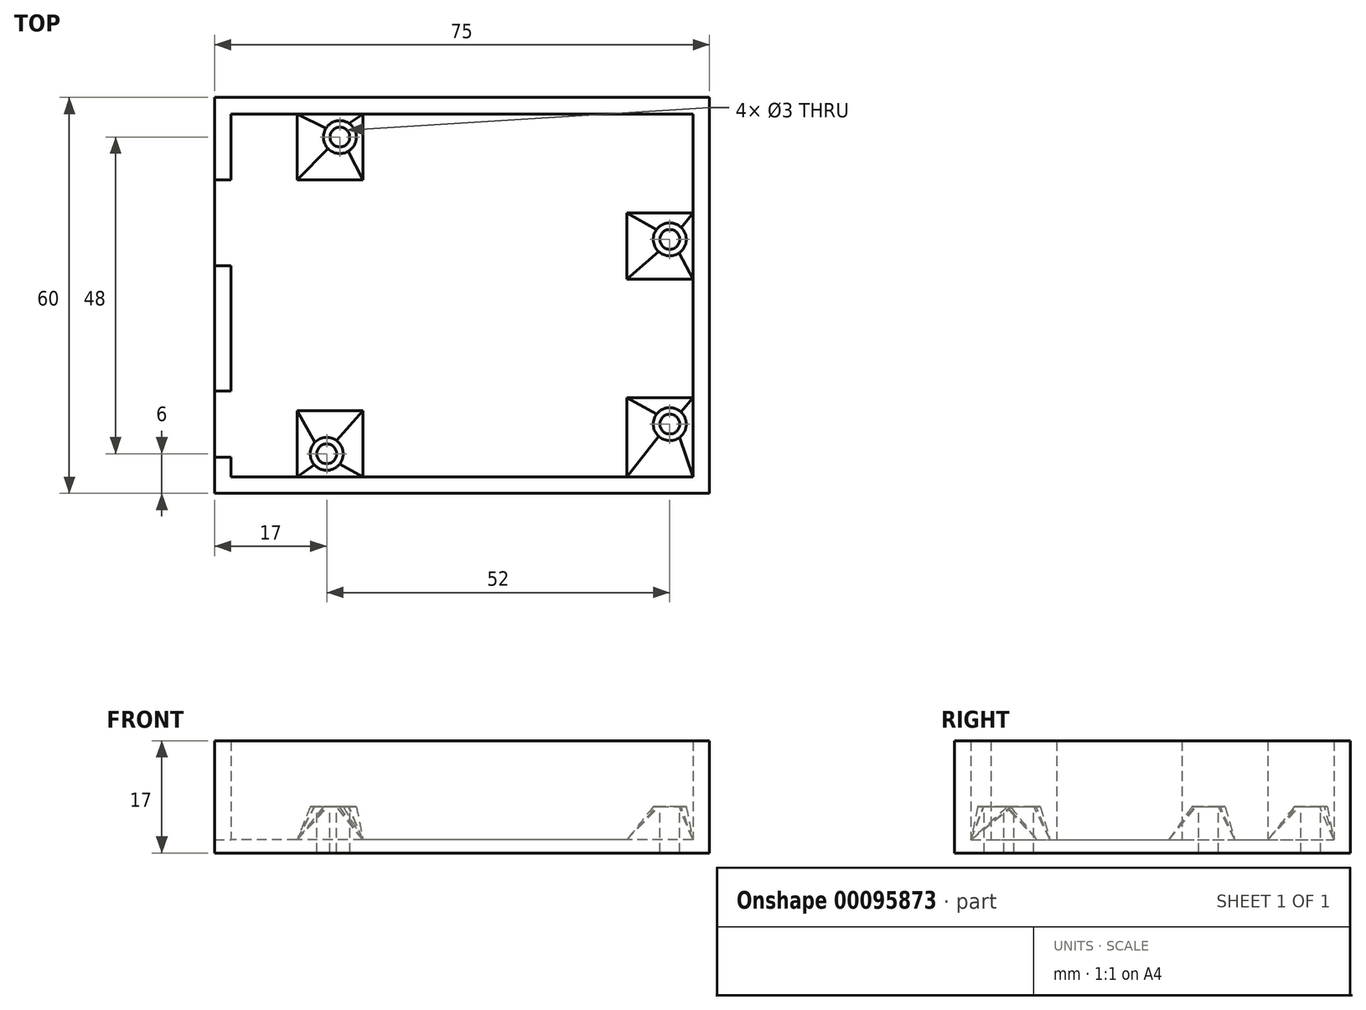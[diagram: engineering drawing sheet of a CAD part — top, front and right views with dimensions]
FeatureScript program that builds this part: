
annotation { "Feature Type Name" : "Feature", "Feature Type Description" : "" }
export const myFeature = defineFeature(function(context is Context, id is Id, definition is map)
    precondition{}
    {
        {
            var Q0;
            Q0=qCreatedBy(makeId("Top.planeOp"),FACE);
            var sketch = newSketch(context, id + "F0", { "sketchPlane" : qUnion([Q0])});
            skLineSegment(sketch, "E0.rect.bottom", {"start": v(37.5, -30) * mm, "end": v(-37.5, -30) * mm});
            skLineSegment(sketch, "E0.rect.top", {"start": v(37.5, 30) * mm, "end": v(-37.5, 30) * mm});
            skLineSegment(sketch, "E0.rect.left", {"start": v(37.5, -30) * mm, "end": v(37.5, 30) * mm});
            skLineSegment(sketch, "E0.rect.right", {"start": v(-37.5, -30) * mm, "end": v(-37.5, 30) * mm});
            skPoint(sketch, "E0.rect.middle", {"position": v(0, 0) * mm});
            skSolve(sketch);
        }
        {
            var Q0;
            Q0=qSketchRegion(id+"F0",true);
            extrude(context, id + "F1", {"entities" : qUnion([Q0]), "depth" : 2 * mm});
        }
        {
            var Q0;
            Q0=makeQuery(id+"F1.opExtrude","CAP_FACE",FACE,{"disambiguationData":[OSD([sQuery(id+"F0.wireOp",EDGE,"E0.rect.bottom"),sQuery(id+"F0.wireOp",EDGE,"E0.rect.top"),sQuery(id+"F0.wireOp",EDGE,"E0.rect.left"),sQuery(id+"F0.wireOp",EDGE,"E0.rect.right")])],"isStart":false});
            var sketch = newSketch(context, id + "F2", { "sketchPlane" : qUnion([Q0])});
            skLineSegment(sketch, "E1.rect.bottom", {"start": v(35, -27.5) * mm, "end": v(-35, -27.5) * mm});
            skLineSegment(sketch, "E1.rect.top", {"start": v(35, 27.5) * mm, "end": v(-35, 27.5) * mm});
            skLineSegment(sketch, "E1.rect.left", {"start": v(35, -27.5) * mm, "end": v(35, 27.5) * mm});
            skLineSegment(sketch, "E1.rect.right", {"start": v(-35, -27.5) * mm, "end": v(-35, 27.5) * mm});
            skPoint(sketch, "E1.rect.middle", {"position": v(0, 0) * mm});
            skLineSegment(sketch, "E2.rect.bottom", {"start": v(37.5, -30) * mm, "end": v(-37.5, -30) * mm});
            skLineSegment(sketch, "E2.rect.top", {"start": v(37.5, 30) * mm, "end": v(-37.5, 30) * mm});
            skLineSegment(sketch, "E2.rect.left", {"start": v(37.5, -30) * mm, "end": v(37.5, 30) * mm});
            skLineSegment(sketch, "E2.rect.right", {"start": v(-37.5, -30) * mm, "end": v(-37.5, 30) * mm});
            skSolve(sketch);
        }
        {
            var Q0;
            Q0=qSketchRegion(id+"F2",true);
            extrude(context, id + "F3", {"entities" : qUnion([Q0]), "operationType" : NewBodyOperationType.ADD, "depth" : 15 * mm});
        }
        {
            var Q0;
            Q0=makeQuery(id+"F1.opExtrude","CAP_FACE",FACE,{"disambiguationData":[OSD([sQuery(id+"F0.wireOp",EDGE,"E0.rect.bottom"),sQuery(id+"F0.wireOp",EDGE,"E0.rect.top"),sQuery(id+"F0.wireOp",EDGE,"E0.rect.left"),sQuery(id+"F0.wireOp",EDGE,"E0.rect.right")])],"isStart":false});
            var sketch = newSketch(context, id + "F4", { "sketchPlane" : qUnion([Q0])});
            skLineSegment(sketch, "E3.bottom", {"start": v(-25, 27.5) * mm, "end": v(-15, 27.5) * mm});
            skLineSegment(sketch, "E3.top", {"start": v(-25, 17.5) * mm, "end": v(-15, 17.5) * mm});
            skLineSegment(sketch, "E3.left", {"start": v(-25, 27.5) * mm, "end": v(-25, 17.5) * mm});
            skLineSegment(sketch, "E3.right", {"start": v(-15, 27.5) * mm, "end": v(-15, 17.5) * mm});
            skLineSegment(sketch, "E4.bottom", {"start": v(-25, -27.5) * mm, "end": v(-15, -27.5) * mm});
            skLineSegment(sketch, "E4.top", {"start": v(-25, -17.5) * mm, "end": v(-15, -17.5) * mm});
            skLineSegment(sketch, "E4.left", {"start": v(-25, -27.5) * mm, "end": v(-25, -17.5) * mm});
            skLineSegment(sketch, "E4.right", {"start": v(-15, -27.5) * mm, "end": v(-15, -17.5) * mm});
            skLineSegment(sketch, "E5.bottom", {"start": v(35, -27.5) * mm, "end": v(25, -27.5) * mm});
            skLineSegment(sketch, "E5.top", {"start": v(35, -15.5) * mm, "end": v(25, -15.5) * mm});
            skLineSegment(sketch, "E5.left", {"start": v(35, -27.5) * mm, "end": v(35, -15.5) * mm});
            skLineSegment(sketch, "E5.right", {"start": v(25, -27.5) * mm, "end": v(25, -15.5) * mm});
            skLineSegment(sketch, "E6.bottom", {"start": v(35, 12.5) * mm, "end": v(25, 12.5) * mm});
            skLineSegment(sketch, "E6.top", {"start": v(35, 2.5) * mm, "end": v(25, 2.5) * mm});
            skLineSegment(sketch, "E6.left", {"start": v(35, 12.5) * mm, "end": v(35, 2.5) * mm});
            skLineSegment(sketch, "E6.right", {"start": v(25, 12.5) * mm, "end": v(25, 2.5) * mm});
            skSolve(sketch);
        }
        {
            var Q0;
            Q0=makeQuery(id+"F4.imprint","IMPRINT",FACE,{"disambiguationData":[TD([[makeQuery(id+"F4.imprint","IMPRINT",EDGE,{"derivedFrom":sQuery(id+"F4.wireOp",EDGE,"E3.top")}),-1.0]])]});
            cPlane(context, id + "F5", {"entities" : qUnion([Q0]), "cplaneType" : CPlaneType.OFFSET, "offset" : 5 * mm, "width" : 150 * mm, "height" : 150 * mm});
        }
        {
            var Q0;
            Q0=qCreatedBy(id+"F5.planeOp",FACE);
            var sketch = newSketch(context, id + "F6", { "sketchPlane" : qUnion([Q0])});
            skArc(sketch, "E7", {"start": v(-17.2, 21.86) * mm, "mid": v(-16, 23.94) * mm, "end": v(-17.1, 26.07) * mm});
            skArc(sketch, "E8", {"start": v(-17.1, 26.07) * mm, "mid": v(-19, 26.45) * mm, "end": v(-20.6, 25.36) * mm});
            skArc(sketch, "E9", {"start": v(-20.6, 25.36) * mm, "mid": v(-20.99, 23.76) * mm, "end": v(-20.3, 22.26) * mm});
            skArc(sketch, "E10", {"start": v(-20.3, 22.26) * mm, "mid": v(-18.82, 21.52) * mm, "end": v(-17.2, 21.86) * mm});
            skArc(sketch, "E11", {"start": v(-22.3, -22.26) * mm, "mid": v(-23, -23.92) * mm, "end": v(-22.4, -25.63) * mm});
            skArc(sketch, "E12", {"start": v(-19.03, -21.98) * mm, "mid": v(-20.71, -21.5) * mm, "end": v(-22.3, -22.26) * mm});
            skArc(sketch, "E13", {"start": v(-18.54, -25.56) * mm, "mid": v(-18.02, -23.66) * mm, "end": v(-19.03, -21.98) * mm});
            skArc(sketch, "E14", {"start": v(-22.4, -25.63) * mm, "mid": v(-20.45, -26.5) * mm, "end": v(-18.54, -25.56) * mm});
            skArc(sketch, "E15", {"start": v(29.8, -21.33) * mm, "mid": v(31.36, -22) * mm, "end": v(32.98, -21.51) * mm});
            skArc(sketch, "E16", {"start": v(29.53, -17.96) * mm, "mid": v(29, -19.7) * mm, "end": v(29.8, -21.33) * mm});
            skArc(sketch, "E17", {"start": v(33.16, -17.63) * mm, "mid": v(31.27, -17.01) * mm, "end": v(29.53, -17.96) * mm});
            skArc(sketch, "E18", {"start": v(32.98, -21.51) * mm, "mid": v(34, -19.61) * mm, "end": v(33.16, -17.63) * mm});
            skArc(sketch, "E19", {"start": v(32.9, 6.43) * mm, "mid": v(34, 8.3) * mm, "end": v(33.23, 10.3) * mm});
            skArc(sketch, "E20", {"start": v(33.23, 10.3) * mm, "mid": v(31.28, 11) * mm, "end": v(29.48, 9.98) * mm});
            skArc(sketch, "E21", {"start": v(29.48, 9.98) * mm, "mid": v(29.01, 8.25) * mm, "end": v(29.82, 6.65) * mm});
            skArc(sketch, "E22", {"start": v(29.82, 6.65) * mm, "mid": v(31.32, 6) * mm, "end": v(32.9, 6.43) * mm});
            skSolve(sketch);
        }
        {
            var Q1;
            Q1=makeQuery(id+"F4.imprint","IMPRINT",FACE,{"disambiguationData":[TD([[makeQuery(id+"F4.imprint","IMPRINT",EDGE,{"derivedFrom":sQuery(id+"F4.wireOp",EDGE,"E3.bottom")}),1.0]])]});
            var Q2;
            Q2=makeQuery(id+"F6.imprint","IMPRINT",FACE,{"disambiguationData":[TD([[makeQuery(id+"F6.imprint","IMPRINT",EDGE,{"derivedFrom":sQuery(id+"F6.wireOp",EDGE,"E7")}),1.0]])]});
            loft(context, id + "F7", {"operationType" : NewBodyOperationType.ADD, "sheetProfilesArray" : [{ "sheetProfileEntities" : qUnion([Q1]) }, { "sheetProfileEntities" : qUnion([Q2]) }]});
        }
        {
            var Q1;
            Q1=makeQuery(id+"F4.imprint","IMPRINT",FACE,{"disambiguationData":[TD([[makeQuery(id+"F4.imprint","IMPRINT",EDGE,{"derivedFrom":sQuery(id+"F4.wireOp",EDGE,"E6.bottom")}),1.0]])]});
            var Q2;
            Q2=makeQuery(id+"F6.imprint","IMPRINT",FACE,{"disambiguationData":[TD([[makeQuery(id+"F6.imprint","IMPRINT",EDGE,{"derivedFrom":sQuery(id+"F6.wireOp",EDGE,"E19")}),1.0]])]});
            loft(context, id + "F8", {"operationType" : NewBodyOperationType.ADD, "sheetProfilesArray" : [{ "sheetProfileEntities" : qUnion([Q1]) }, { "sheetProfileEntities" : qUnion([Q2]) }]});
        }
        {
            var Q1;
            Q1=makeQuery(id+"F4.imprint","IMPRINT",FACE,{"disambiguationData":[TD([[makeQuery(id+"F4.imprint","IMPRINT",EDGE,{"derivedFrom":sQuery(id+"F4.wireOp",EDGE,"E5.bottom")}),-1.0]])]});
            var Q2;
            Q2=makeQuery(id+"F6.imprint","IMPRINT",FACE,{"disambiguationData":[TD([[makeQuery(id+"F6.imprint","IMPRINT",EDGE,{"derivedFrom":sQuery(id+"F6.wireOp",EDGE,"E15")}),1.0]])]});
            loft(context, id + "F9", {"operationType" : NewBodyOperationType.ADD, "sheetProfilesArray" : [{ "sheetProfileEntities" : qUnion([Q1]) }, { "sheetProfileEntities" : qUnion([Q2]) }]});
        }
        {
            var Q1;
            Q1=makeQuery(id+"F4.imprint","IMPRINT",FACE,{"disambiguationData":[TD([[makeQuery(id+"F4.imprint","IMPRINT",EDGE,{"derivedFrom":sQuery(id+"F4.wireOp",EDGE,"E4.bottom")}),-1.0]])]});
            var Q2;
            Q2=makeQuery(id+"F6.imprint","IMPRINT",FACE,{"disambiguationData":[TD([[makeQuery(id+"F6.imprint","IMPRINT",EDGE,{"derivedFrom":sQuery(id+"F6.wireOp",EDGE,"E11")}),1.0]])]});
            loft(context, id + "F10", {"operationType" : NewBodyOperationType.ADD, "sheetProfilesArray" : [{ "sheetProfileEntities" : qUnion([Q1]) }, { "sheetProfileEntities" : qUnion([Q2]) }]});
        }
        {
            var Q0;
            Q0=sQuery(id+"F6.wireOp",VERTEX,"E8.center");
            var Q1;
            Q1=sQuery(id+"F6.wireOp",VERTEX,"E19.center");
            var Q2;
            Q2=sQuery(id+"F6.wireOp",VERTEX,"E17.center");
            var Q3;
            Q3=sQuery(id+"F6.wireOp",VERTEX,"E12.center");
            var Q4;
            Q4=makeQuery(id+"F1.opExtrude","SWEPT_BODY",BODY,{"disambiguationData":[OSD([sQuery(id+"F0.wireOp",EDGE,"E0.rect.bottom"),sQuery(id+"F0.wireOp",EDGE,"E0.rect.top"),sQuery(id+"F0.wireOp",EDGE,"E0.rect.left"),sQuery(id+"F0.wireOp",EDGE,"E0.rect.right")])]});
            hole(context, id + "F11", {"style" : HoleStyle.SIMPLE, "holeDiameter" : 3 * mm, "endStyle" : HoleEndStyle.THROUGH, "locations" : qUnion([Q0, Q1, Q2, Q3]), "scope" : qUnion([Q4])});
        }
        {
            var Q0;
            Q0=makeQuery(id+"F3.opExtrude","SWEPT_FACE",FACE,{"disambiguationData":[OSD([sQuery(id+"F2.wireOp",EDGE,"E1.rect.right")])]});
            var sketch = newSketch(context, id + "F12", { "sketchPlane" : qUnion([Q0])});
            skLineSegment(sketch, "E23.bottom", {"start": v(-24.5, 17) * mm, "end": v(-14.5, 17) * mm});
            skLineSegment(sketch, "E23.top", {"start": v(-24.5, 2) * mm, "end": v(-14.5, 2) * mm});
            skLineSegment(sketch, "E23.left", {"start": v(-24.5, 17) * mm, "end": v(-24.5, 2) * mm});
            skLineSegment(sketch, "E23.right", {"start": v(-14.5, 17) * mm, "end": v(-14.5, 2) * mm});
            skLineSegment(sketch, "E24.bottom", {"start": v(4.5, 17) * mm, "end": v(17.5, 17) * mm});
            skLineSegment(sketch, "E24.top", {"start": v(4.5, 2) * mm, "end": v(17.5, 2) * mm});
            skLineSegment(sketch, "E24.left", {"start": v(4.5, 17) * mm, "end": v(4.5, 2) * mm});
            skLineSegment(sketch, "E24.right", {"start": v(17.5, 17) * mm, "end": v(17.5, 2) * mm});
            skSolve(sketch);
        }
        {
            var Q0;
            Q0=qSketchRegion(id+"F12",true);
            extrude(context, id + "F13", {"entities" : qUnion([Q0]), "operationType" : NewBodyOperationType.REMOVE, "endBound" : BoundingType.UP_TO_NEXT, "oppositeDirection" : true, "depth" : 25 * mm});
        }
    });
